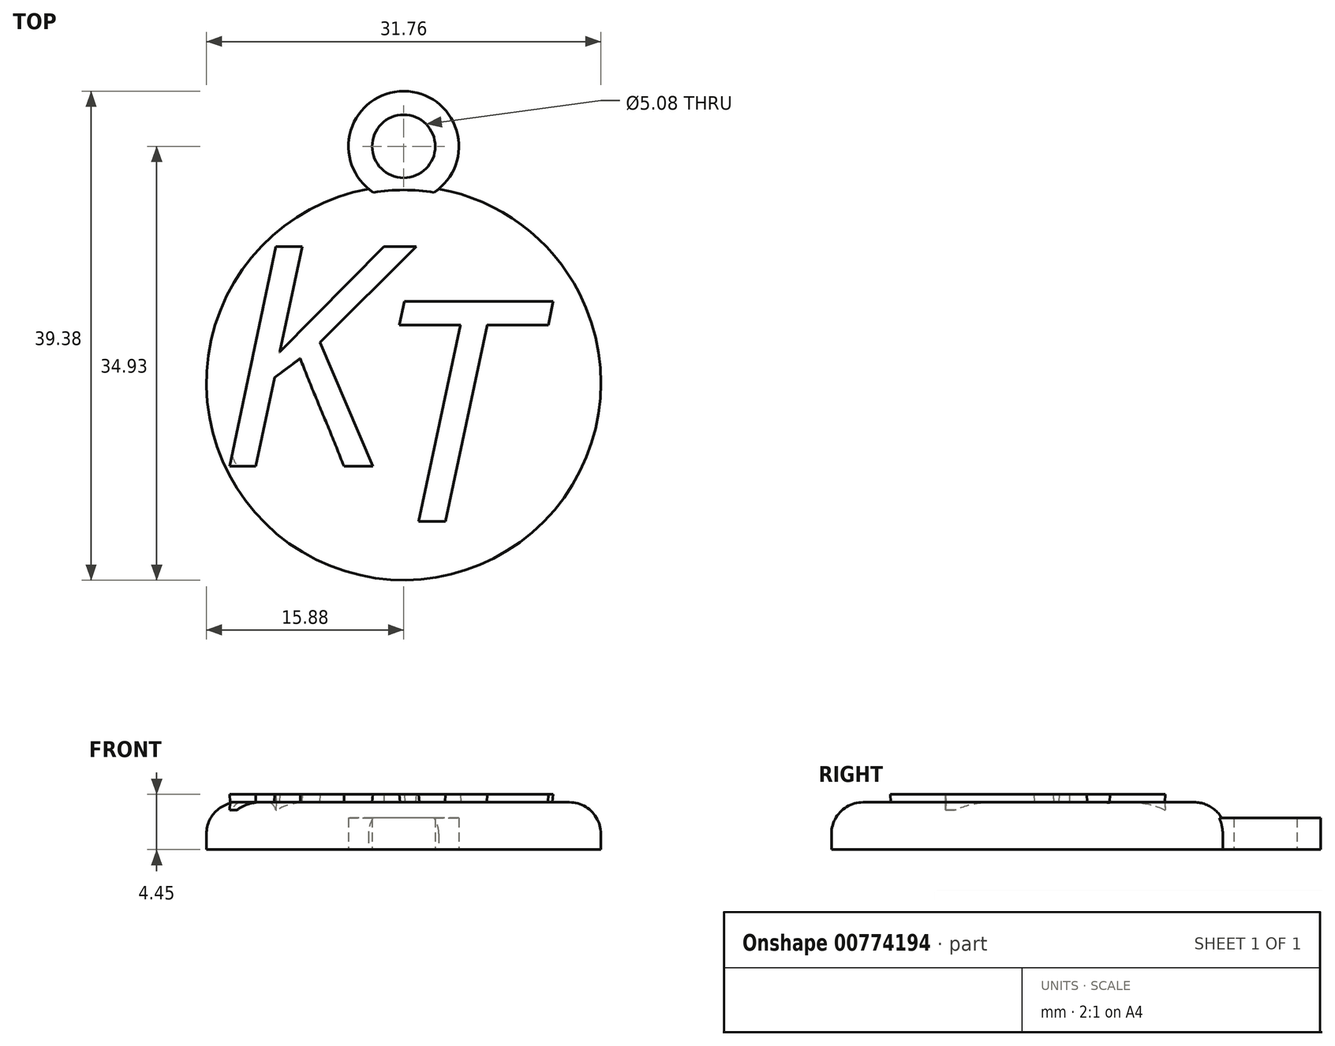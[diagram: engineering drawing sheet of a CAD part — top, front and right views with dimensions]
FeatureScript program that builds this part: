
annotation { "Feature Type Name" : "Feature", "Feature Type Description" : "" }
export const myFeature = defineFeature(function(context is Context, id is Id, definition is map)
    precondition{}
    {
        {
            var Q0;
            Q0=qCreatedBy(makeId("Top.planeOp"),FACE);
            var sketch = newSketch(context, id + "F0", { "sketchPlane" : qUnion([Q0])});
            skCircle(sketch, "E0", {"center": v(0, 0) * mm, "radius": 15.88 * mm});
            skSolve(sketch);
        }
        {
            var Q0;
            Q0 = qSketchRegion(id + "F0", true);
            extrude(context, id + "F1", {"entities" : qUnion([Q0]), "depth" : 3.8 * mm, "offsetDistance" : 25.4 * mm});
        }
        {
            var Q0;
            Q0=makeQuery(id+"F1.opExtrude","CAP_EDGE",EDGE,{"disambiguationData":[OSD([sQuery(id+"F0.wireOp",EDGE,"E0")])],"isStart":false});
            fillet(context, id + "F2", {"entities" : qUnion([Q0]), "radius" : 2.54 * mm, "tangentPropagation" : true, "allowEdgeOverflow" : false});
        }
        {
            var Q0;
            Q0=qCreatedBy(makeId("Top.planeOp"),FACE);
            var sketch = newSketch(context, id + "F3", { "sketchPlane" : qUnion([Q0])});
            skPoint(sketch, "E1", {"position": v(0, 15.88) * mm});
            skPoint(sketch, "E2", {"position": v(0, 19.05) * mm});
            skCircle(sketch, "E3", {"center": v(0, 19.05) * mm, "radius": 4.45 * mm});
            skCircle(sketch, "E4", {"center": v(0, 19.05) * mm, "radius": 2.54 * mm});
            skSolve(sketch);
        }
        {
            var Q0;
            Q0=makeQuery(id+"F3.imprint","IMPRINT",FACE,{"disambiguationData":[TD([[makeQuery(id+"F3.imprint","IMPRINT",EDGE,{"derivedFrom":sQuery(id+"F3.wireOp",EDGE,"E3")}),1.0]])]});
            extrude(context, id + "F4", {"entities" : qUnion([Q0]), "operationType" : NewBodyOperationType.ADD, "depth" : 2.54 * mm, "offsetDistance" : 25.4 * mm});
        }
        {
            var Q0;
            Q0=makeQuery(id+"F1.opExtrude","CAP_FACE",FACE,{"disambiguationData":[OSD([sQuery(id+"F0.wireOp",EDGE,"E0")])],"isStart":false});
            var sketch = newSketch(context, id + "F5", { "sketchPlane" : qUnion([Q0])});
            skText(sketch, "E5", { "text": "K", "fontName": "OpenSans-Italic.ttf"});
            skText(sketch, "E6", { "text": "T", "fontName": "OpenSans-Italic.ttf"});
            skPoint(sketch, "E7", {"position": v(0, 13.33) * mm});
            skPoint(sketch, "E8", {"position": v(0, -13.33) * mm});
            skPoint(sketch, "E9", {"position": v(0, -6.67) * mm});
            skPoint(sketch, "E10", {"position": v(0, 6.67) * mm});
            skPoint(sketch, "E11", {"position": v(-2.54, 6.67) * mm});
            skPoint(sketch, "E12", {"position": v(2.54, -6.67) * mm});
            skLineSegment(sketch, "E13", {"start": v(-2.54, 6.67) * mm, "end": v(0, 6.67) * mm});
            skLineSegment(sketch, "E14", {"start": v(0, -6.67) * mm, "end": v(2.54, -6.67) * mm});
            const initialGuessF5  = {"E5": [-0.01501, -0.00667, 1, 0, 0.01778], "E6": [-0.00254, -0.01111, 1, 0, 0.01778]};
            skSetInitialGuess(sketch, initialGuessF5);
            skSolve(sketch);
        }
        {
            var Q0;
            Q0 = qSketchRegion(id + "F5", true);
            extrude(context, id + "F6", {"entities" : qUnion([Q0]), "operationType" : NewBodyOperationType.ADD, "endBound" : BoundingType.SYMMETRIC, "depth" : 1.27 * mm, "offsetDistance" : 25.4 * mm, "hasDraft" : true, "draftAngle" : 3 * degree});
        }
    });
